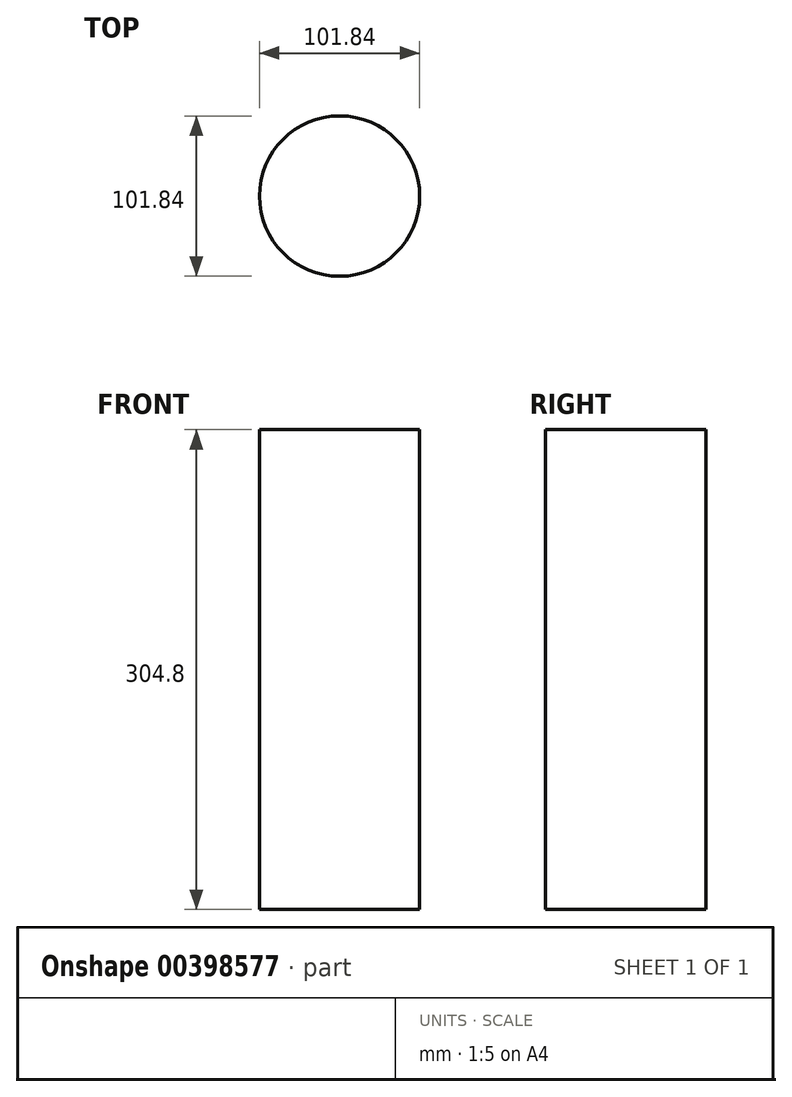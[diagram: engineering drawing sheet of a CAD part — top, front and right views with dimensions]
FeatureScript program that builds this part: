
annotation { "Feature Type Name" : "Feature", "Feature Type Description" : "" }
export const myFeature = defineFeature(function(context is Context, id is Id, definition is map)
    precondition{}
    {
        {
            var Q0;
            Q0=qCreatedBy(makeId("Top.planeOp"),FACE);
            var sketch = newSketch(context, id + "F0", { "sketchPlane" : qUnion([Q0])});
            skCircle(sketch, "E0", {"center": v(0, 0) * mm, "radius": 50.92 * mm});
            skSolve(sketch);
        }
        {
            var Q0;
            Q0=makeQuery(id+"F0.imprint","IMPRINT",FACE,{"disambiguationData":[TD([[makeQuery(id+"F0.imprint","IMPRINT",EDGE,{"derivedFrom":sQuery(id+"F0.wireOp",EDGE,"E0")}),1.0]])]});
            extrude(context, id + "F1", {"entities" : qUnion([Q0]), "depth" : 304.8 * mm});
        }
    });
